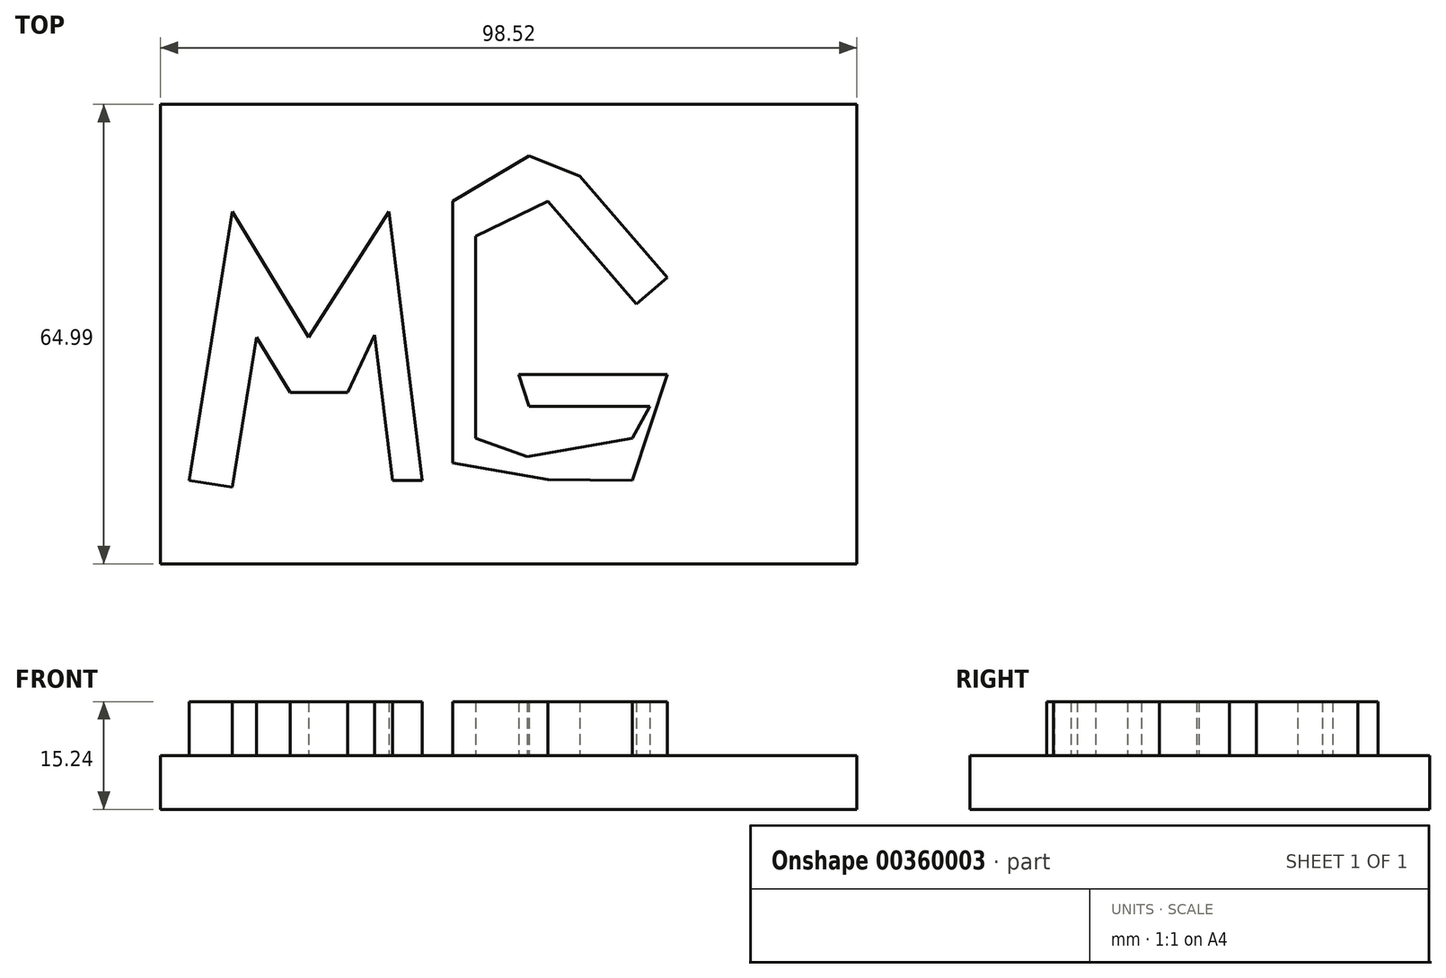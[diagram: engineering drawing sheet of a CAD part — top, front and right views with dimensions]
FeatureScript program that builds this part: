
annotation { "Feature Type Name" : "Feature", "Feature Type Description" : "" }
export const myFeature = defineFeature(function(context is Context, id is Id, definition is map)
    precondition{}
    {
        {
            var Q0;
            Q0=qCreatedBy(makeId("Top.planeOp"),FACE);
            var sketch = newSketch(context, id + "F0", { "sketchPlane" : qUnion([Q0])});
            skLineSegment(sketch, "E0", {"start": v(-67.62, 0) * mm, "end": v(-61.5, 38.04) * mm});
            skLineSegment(sketch, "E1", {"start": v(-61.5, 38.04) * mm, "end": v(-50.72, 20.26) * mm});
            skLineSegment(sketch, "E2", {"start": v(-50.72, 20.26) * mm, "end": v(-39.35, 38.04) * mm});
            skLineSegment(sketch, "E3", {"start": v(-39.35, 38.04) * mm, "end": v(-34.69, 0) * mm});
            skLineSegment(sketch, "E4", {"start": v(-67.62, 0) * mm, "end": v(-61.5, -0.98) * mm});
            skLineSegment(sketch, "E5", {"start": v(-61.5, -0.98) * mm, "end": v(-58.08, 20.26) * mm});
            skLineSegment(sketch, "E6", {"start": v(-58.08, 20.26) * mm, "end": v(-53.34, 12.44) * mm});
            skLineSegment(sketch, "E7", {"start": v(-53.34, 12.44) * mm, "end": v(-45.18, 12.44) * mm});
            skLineSegment(sketch, "E8", {"start": v(-45.18, 12.44) * mm, "end": v(-41.39, 20.55) * mm});
            skLineSegment(sketch, "E9", {"start": v(-41.39, 20.55) * mm, "end": v(-38.87, 0) * mm});
            skLineSegment(sketch, "E10", {"start": v(-38.87, 0) * mm, "end": v(-34.69, 0) * mm});
            skLineSegment(sketch, "E11", {"start": v(-4.37, 24.92) * mm, "end": v(-16.9, 39.5) * mm});
            skLineSegment(sketch, "E12", {"start": v(-16.9, 39.5) * mm, "end": v(-27.1, 34.54) * mm});
            skLineSegment(sketch, "E13", {"start": v(-27.1, 34.54) * mm, "end": v(-27.1, 21.71) * mm});
            skLineSegment(sketch, "E14", {"start": v(-27.1, 21.71) * mm, "end": v(-27.1, 5.98) * mm});
            skLineSegment(sketch, "E15", {"start": v(-27.1, 5.98) * mm, "end": v(-19.82, 3.35) * mm});
            skLineSegment(sketch, "E16", {"start": v(-19.82, 3.35) * mm, "end": v(-4.96, 5.98) * mm});
            skLineSegment(sketch, "E17", {"start": v(-4.96, 5.98) * mm, "end": v(0, 15.01) * mm});
            skLineSegment(sketch, "E18", {"start": v(0, 15.01) * mm, "end": v(-20.99, 15.01) * mm});
            skLineSegment(sketch, "E19", {"start": v(-4.37, 24.92) * mm, "end": v(0, 28.68) * mm});
            skLineSegment(sketch, "E20", {"start": v(0, 28.68) * mm, "end": v(-12.34, 43.03) * mm});
            skLineSegment(sketch, "E21", {"start": v(-12.34, 43.03) * mm, "end": v(-19.53, 45.9) * mm});
            skLineSegment(sketch, "E22", {"start": v(-19.53, 45.9) * mm, "end": v(-30.31, 39.5) * mm});
            skLineSegment(sketch, "E23", {"start": v(-30.31, 39.5) * mm, "end": v(-30.31, 2.48) * mm});
            skLineSegment(sketch, "E24", {"start": v(-30.31, 2.48) * mm, "end": v(-16.9, 0.15) * mm});
            skLineSegment(sketch, "E25", {"start": v(-16.9, 0.15) * mm, "end": v(-4.96, 0) * mm});
            skLineSegment(sketch, "E26", {"start": v(-4.96, 0) * mm, "end": v(0, 15.01) * mm});
            skLineSegment(sketch, "E27", {"start": v(-20.99, 15.01) * mm, "end": v(-19.53, 10.5) * mm});
            skPoint(sketch, "E27.endSnap0", {"position": v(-2.48, 10.5) * mm});
            skLineSegment(sketch, "E28", {"start": v(-19.53, 10.5) * mm, "end": v(-2.48, 10.5) * mm});
            skSolve(sketch);
        }
        {
            var Q0;
            Q0 = qSketchRegion(id + "F0", true);
            extrude(context, id + "F1", {"entities" : qUnion([Q0]), "depth" : 7.62 * mm});
        }
        {
            var Q0;
            Q0=qCreatedBy(makeId("Top.planeOp"),FACE);
            var sketch = newSketch(context, id + "F2", { "sketchPlane" : qUnion([Q0])});
            skLineSegment(sketch, "E29.bottom", {"start": v(-71.7, 53.2) * mm, "end": v(26.82, 53.2) * mm});
            skLineSegment(sketch, "E29.top", {"start": v(-71.7, -11.8) * mm, "end": v(26.82, -11.8) * mm});
            skLineSegment(sketch, "E29.left", {"start": v(-71.7, 53.2) * mm, "end": v(-71.7, -11.8) * mm});
            skLineSegment(sketch, "E29.right", {"start": v(26.82, 53.2) * mm, "end": v(26.82, -11.8) * mm});
            skSolve(sketch);
        }
        {
            var Q0;
            Q0 = qSketchRegion(id + "F2", true);
            extrude(context, id + "F3", {"entities" : qUnion([Q0]), "oppositeDirection" : true, "depth" : 7.62 * mm});
        }
    });
